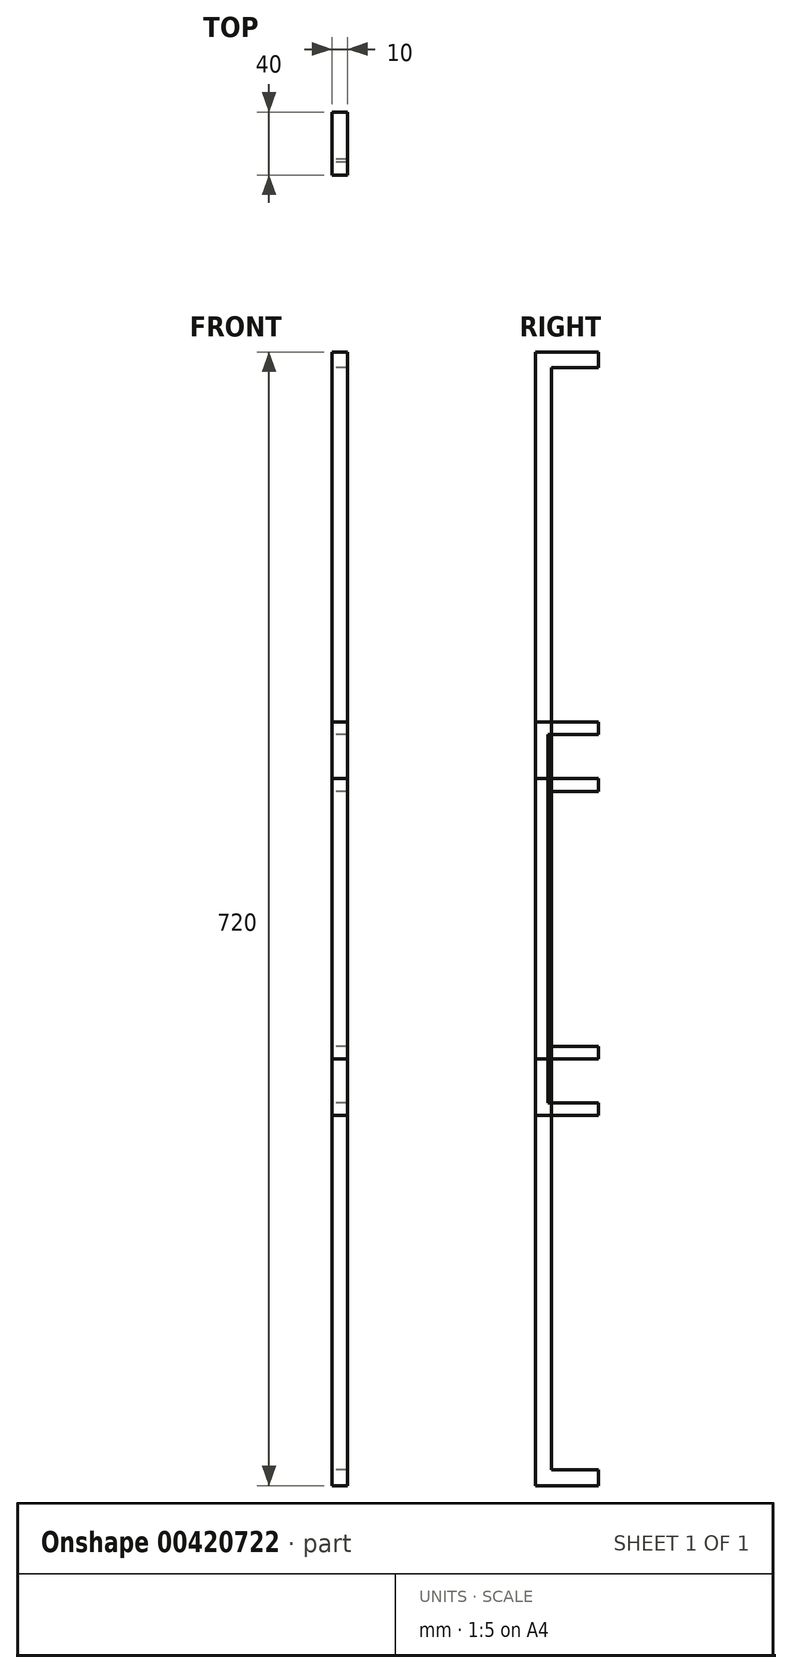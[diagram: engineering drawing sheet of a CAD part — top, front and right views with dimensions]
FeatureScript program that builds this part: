
annotation { "Feature Type Name" : "Feature", "Feature Type Description" : "" }
export const myFeature = defineFeature(function(context is Context, id is Id, definition is map)
    precondition{}
    {
        {
            var Q0;
            Q0=qCreatedBy(makeId("Right.planeOp"),FACE);
            var sketch = newSketch(context, id + "F0", { "sketchPlane" : qUnion([Q0])});
            skLineSegment(sketch, "E0", {"start": v(0, 117) * mm, "end": v(-32, 117) * mm});
            skLineSegment(sketch, "E1", {"start": v(-32, 117) * mm, "end": v(-32, -117) * mm});
            skLineSegment(sketch, "E2", {"start": v(-32, -117) * mm, "end": v(0, -117) * mm});
            skLineSegment(sketch, "E3.0", {"start": v(-40, -125) * mm, "end": v(0, -125) * mm});
            skLineSegment(sketch, "E3.1", {"start": v(-40, 125) * mm, "end": v(-40, -125) * mm});
            skLineSegment(sketch, "E3.2", {"start": v(0, 125) * mm, "end": v(-40, 125) * mm});
            skLineSegment(sketch, "E4", {"start": v(0, 125) * mm, "end": v(0, 117) * mm});
            skLineSegment(sketch, "E5", {"start": v(0, -117) * mm, "end": v(0, -125) * mm});
            skSolve(sketch);
        }
        {
            var Q0;
            Q0 = qSketchRegion(id + "F0", true);
            extrude(context, id + "F1", {"entities" : qUnion([Q0]), "depth" : 10 * mm, "symmetric" : true});
        }
        {
            var Q0;
            Q0=qCreatedBy(makeId("Right.planeOp"),FACE);
            var sketch = newSketch(context, id + "F2", { "sketchPlane" : qUnion([Q0])});
            skLineSegment(sketch, "E6", {"start": v(0, 350) * mm, "end": v(-30, 350) * mm});
            skLineSegment(sketch, "E7", {"start": v(-30, 350) * mm, "end": v(-30, -350) * mm});
            skLineSegment(sketch, "E8", {"start": v(-30, -350) * mm, "end": v(0, -350) * mm});
            skLineSegment(sketch, "E9.0", {"start": v(-40, -360) * mm, "end": v(0, -360) * mm});
            skLineSegment(sketch, "E9.1", {"start": v(-40, 360) * mm, "end": v(-40, -360) * mm});
            skLineSegment(sketch, "E9.2", {"start": v(0, 360) * mm, "end": v(-40, 360) * mm});
            skLineSegment(sketch, "E10", {"start": v(0, 360) * mm, "end": v(0, 350) * mm});
            skLineSegment(sketch, "E11", {"start": v(0, -350) * mm, "end": v(0, -360) * mm});
            skSolve(sketch);
        }
        {
            var Q0;
            Q0 = qSketchRegion(id + "F2", true);
            extrude(context, id + "F3", {"entities" : qUnion([Q0]), "depth" : 10 * mm, "symmetric" : true});
        }
        {
            var Q0;
            Q0=qCreatedBy(makeId("Right.planeOp"),FACE);
            var sketch = newSketch(context, id + "F4", { "sketchPlane" : qUnion([Q0])});
            skLineSegment(sketch, "E12", {"start": v(0, 81) * mm, "end": v(-32, 81) * mm});
            skLineSegment(sketch, "E13", {"start": v(-32, 81) * mm, "end": v(-32, -81) * mm});
            skLineSegment(sketch, "E14", {"start": v(-32, -81) * mm, "end": v(0, -81) * mm});
            skLineSegment(sketch, "E15.0", {"start": v(-40, -89) * mm, "end": v(0, -89) * mm});
            skLineSegment(sketch, "E15.1", {"start": v(-40, 89) * mm, "end": v(-40, -89) * mm});
            skLineSegment(sketch, "E15.2", {"start": v(0, 89) * mm, "end": v(-40, 89) * mm});
            skLineSegment(sketch, "E16", {"start": v(0, 89) * mm, "end": v(0, 81) * mm});
            skLineSegment(sketch, "E17", {"start": v(0, -81) * mm, "end": v(0, -89) * mm});
            skSolve(sketch);
        }
        {
            var Q0;
            Q0 = qSketchRegion(id + "F4", true);
            extrude(context, id + "F5", {"entities" : qUnion([Q0]), "depth" : 10 * mm, "symmetric" : true});
        }
        {
            var Q0;
            Q0=qCreatedBy(makeId("Right.planeOp"),FACE);
            var sketch = newSketch(context, id + "F6", { "sketchPlane" : qUnion([Q0])});
            skLineSegment(sketch, "E18", {"start": v(0, 81) * mm, "end": v(-32, 81) * mm});
            skLineSegment(sketch, "E19", {"start": v(-32, 81) * mm, "end": v(-32, -81) * mm});
            skLineSegment(sketch, "E20", {"start": v(-32, -81) * mm, "end": v(0, -81) * mm});
            skLineSegment(sketch, "E21.0", {"start": v(-40, -89) * mm, "end": v(0, -89) * mm});
            skLineSegment(sketch, "E21.1", {"start": v(-40, 89) * mm, "end": v(-40, -89) * mm});
            skLineSegment(sketch, "E21.2", {"start": v(0, 89) * mm, "end": v(-40, 89) * mm});
            skLineSegment(sketch, "E22", {"start": v(0, 89) * mm, "end": v(0, 81) * mm});
            skLineSegment(sketch, "E23", {"start": v(0, -81) * mm, "end": v(0, -89) * mm});
            skSolve(sketch);
        }
        {
            var Q0;
            Q0 = qSketchRegion(id + "F6", true);
            extrude(context, id + "F7", {"entities" : qUnion([Q0]), "depth" : 10 * mm, "symmetric" : true});
        }
    });
